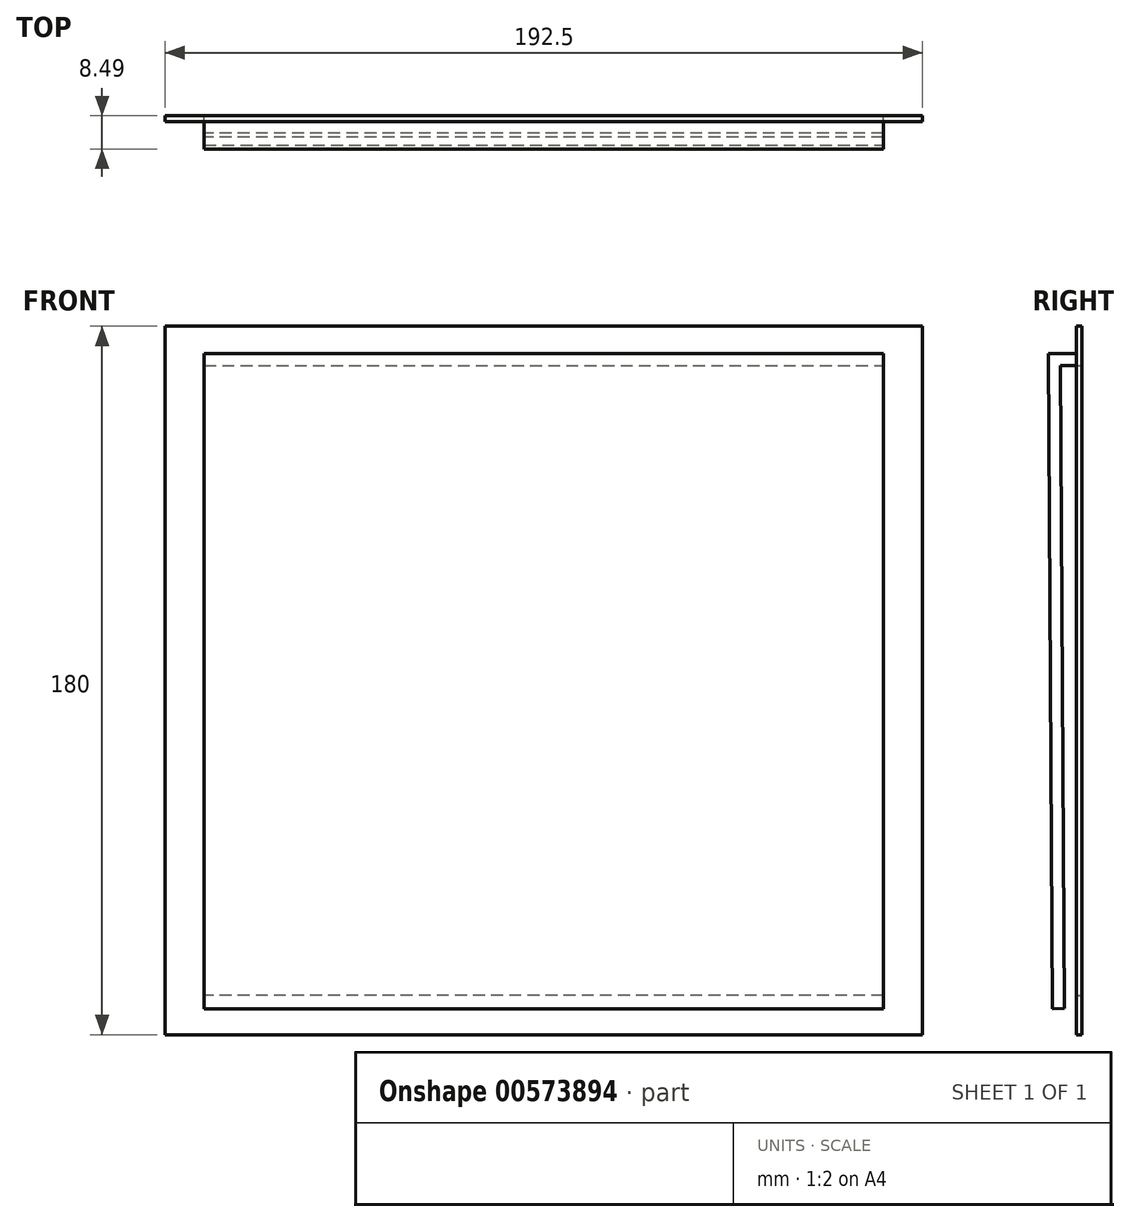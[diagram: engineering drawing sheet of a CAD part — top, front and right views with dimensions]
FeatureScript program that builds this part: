
annotation { "Feature Type Name" : "Feature", "Feature Type Description" : "" }
export const myFeature = defineFeature(function(context is Context, id is Id, definition is map)
    precondition{}
    {
        {
            var Q0;
            Q0=qCreatedBy(makeId("Front.planeOp"),FACE);
            var sketch = newSketch(context, id + "F0", { "sketchPlane" : qUnion([Q0])});
            skLineSegment(sketch, "E0.bottom", {"start": v(96.25, 90) * mm, "end": v(-96.25, 90) * mm});
            skLineSegment(sketch, "E0.top", {"start": v(96.25, -90) * mm, "end": v(-96.25, -90) * mm});
            skLineSegment(sketch, "E0.left", {"start": v(96.25, 90) * mm, "end": v(96.25, -90) * mm});
            skLineSegment(sketch, "E0.right", {"start": v(-96.25, 90) * mm, "end": v(-96.25, -90) * mm});
            skPoint(sketch, "E0.middle", {"position": v(0, 0) * mm});
            skSolve(sketch);
        }
        {
            var Q0;
            Q0=makeQuery(id+"F0.imprint","IMPRINT",FACE,{"disambiguationData":[TD([[makeQuery(id+"F0.imprint","IMPRINT",EDGE,{"derivedFrom":sQuery(id+"F0.wireOp",EDGE,"E0.bottom")}),1.0]])]});
            extrude(context, id + "F1", {"entities" : qUnion([Q0]), "depth" : 1.5 * mm, "offsetDistance" : 25 * mm});
        }
        {
            var Q0;
            Q0=makeQuery(id+"F1.opExtrude","CAP_FACE",FACE,{"disambiguationData":[OSD([sQuery(id+"F0.wireOp",EDGE,"E0.bottom"),sQuery(id+"F0.wireOp",EDGE,"E0.top"),sQuery(id+"F0.wireOp",EDGE,"E0.left"),sQuery(id+"F0.wireOp",EDGE,"E0.right")])],"isStart":true});
            var sketch = newSketch(context, id + "F2", { "sketchPlane" : qUnion([Q0])});
            skLineSegment(sketch, "E1.bottom", {"start": v(86.25, 80) * mm, "end": v(-86.25, 80) * mm});
            skLineSegment(sketch, "E1.top", {"start": v(86.25, -80) * mm, "end": v(-86.25, -80) * mm});
            skLineSegment(sketch, "E1.left", {"start": v(86.25, 80) * mm, "end": v(86.25, -80) * mm});
            skLineSegment(sketch, "E1.right", {"start": v(-86.25, 80) * mm, "end": v(-86.25, -80) * mm});
            skPoint(sketch, "E1.middle", {"position": v(0, 0) * mm});
            skSolve(sketch);
        }
        {
            var Q0;
            Q0 = qSketchRegion(id + "F2", true);
            var Q1;
            Q1=makeQuery(id+"F1.opExtrude","CAP_FACE",FACE,{"disambiguationData":[OSD([sQuery(id+"F0.wireOp",EDGE,"E0.bottom"),sQuery(id+"F0.wireOp",EDGE,"E0.top"),sQuery(id+"F0.wireOp",EDGE,"E0.left"),sQuery(id+"F0.wireOp",EDGE,"E0.right")])],"isStart":false});
            extrude(context, id + "F3", {"entities" : qUnion([Q0]), "operationType" : NewBodyOperationType.REMOVE, "endBound" : BoundingType.THROUGH_ALL, "oppositeDirection" : true, "depth" : 25 * mm, "endBoundEntityFace" : qUnion([Q1]), "offsetDistance" : 25 * mm});
        }
        {
            var Q0;
            Q0=makeQuery(id+"F1.opExtrude","CAP_FACE",FACE,{"disambiguationData":[OSD([sQuery(id+"F0.wireOp",EDGE,"E0.bottom"),sQuery(id+"F0.wireOp",EDGE,"E0.top"),sQuery(id+"F0.wireOp",EDGE,"E0.left"),sQuery(id+"F0.wireOp",EDGE,"E0.right")])],"isStart":false});
            var sketch = newSketch(context, id + "F4", { "sketchPlane" : qUnion([Q0])});
            skLineSegment(sketch, "E2.bottom", {"start": v(-86.25, 80) * mm, "end": v(86.25, 80) * mm});
            skLineSegment(sketch, "E2.top", {"start": v(-86.25, 83) * mm, "end": v(86.25, 83) * mm});
            skLineSegment(sketch, "E2.left", {"start": v(-86.25, 80) * mm, "end": v(-86.25, 83) * mm});
            skLineSegment(sketch, "E2.right", {"start": v(86.25, 80) * mm, "end": v(86.25, 83) * mm});
            skSolve(sketch);
        }
        {
            var Q0;
            Q0=qCreatedBy(makeId("Right.planeOp"),FACE);
            var sketch = newSketch(context, id + "F5", { "sketchPlane" : qUnion([Q0])});
            skLineSegment(sketch, "E3", {"start": v(-1.5, 82.52) * mm, "end": v(-8, 82.52) * mm});
            skLineSegment(sketch, "E4", {"start": v(-8, 82.52) * mm, "end": v(-7, -83.4) * mm});
            skSolve(sketch);
        }
        {
            var Q0;
            Q0=makeQuery(id+"F4.imprint","IMPRINT",FACE,{"disambiguationData":[TD([[makeQuery(id+"F4.imprint","IMPRINT",EDGE,{"derivedFrom":sQuery(id+"F4.wireOp",EDGE,"E2.bottom")}),-1.0]])]});
            var Q1;
            Q1=sQuery(id+"F5.wireOp",EDGE,"E3");
            var Q2;
            Q2=sQuery(id+"F5.wireOp",EDGE,"E4");
            sweep(context, id + "F6", {"operationType" : NewBodyOperationType.ADD, "profiles" : qUnion([Q0]), "path" : qUnion([Q1, Q2])});
        }
    });
